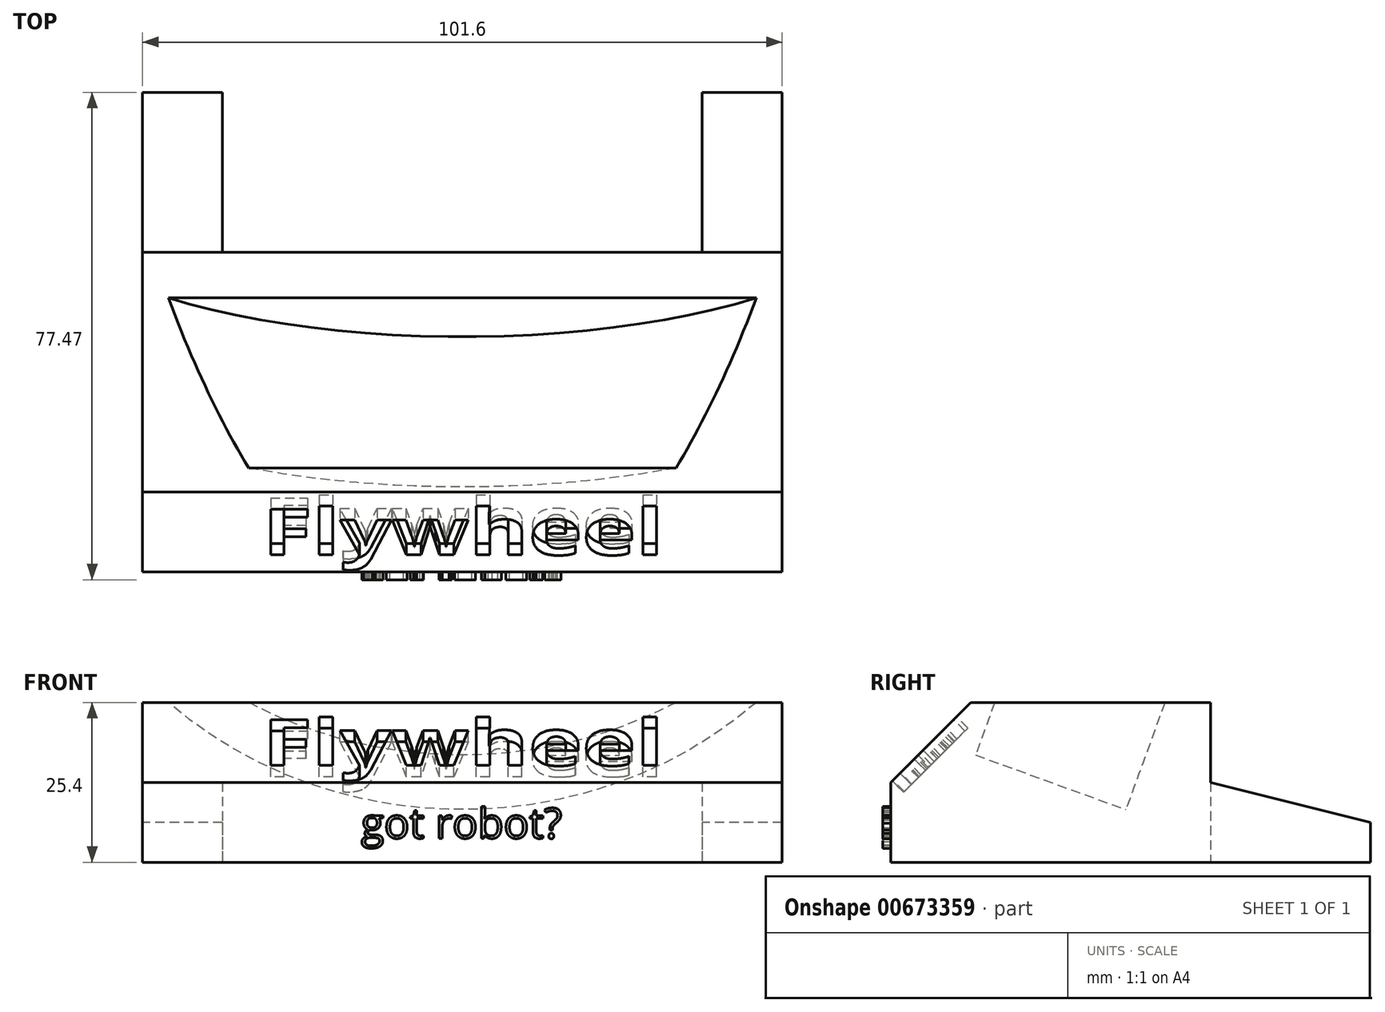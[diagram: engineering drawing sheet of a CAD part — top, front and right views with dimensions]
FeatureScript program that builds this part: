
annotation { "Feature Type Name" : "Feature", "Feature Type Description" : "" }
export const myFeature = defineFeature(function(context is Context, id is Id, definition is map)
    precondition{}
    {
        {
            var Q0;
            Q0=qCreatedBy(makeId("Top.planeOp"),FACE);
            var sketch = newSketch(context, id + "F0", { "sketchPlane" : qUnion([Q0])});
            skLineSegment(sketch, "E0.bottom", {"start": v(-50.8, 25.4) * mm, "end": v(50.8, 25.4) * mm});
            skLineSegment(sketch, "E0.top", {"start": v(-50.8, -25.4) * mm, "end": v(50.8, -25.4) * mm});
            skLineSegment(sketch, "E0.left", {"start": v(-50.8, 25.4) * mm, "end": v(-50.8, -25.4) * mm});
            skLineSegment(sketch, "E0.right", {"start": v(50.8, 25.4) * mm, "end": v(50.8, -25.4) * mm});
            skPoint(sketch, "E0.middle", {"position": v(0, 0) * mm});
            skLineSegment(sketch, "E1.top", {"start": v(-50.8, 0) * mm, "end": v(50.8, 0) * mm});
            skLineSegment(sketch, "E1.left", {"start": v(-50.8, 25.4) * mm, "end": v(-50.8, 0) * mm});
            skLineSegment(sketch, "E1.right", {"start": v(50.8, 25.4) * mm, "end": v(50.8, 0) * mm});
            skLineSegment(sketch, "E2.bottom", {"start": v(-38.1, 25.4) * mm, "end": v(38.1, 25.4) * mm});
            skLineSegment(sketch, "E2.top", {"start": v(-38.1, 50.8) * mm, "end": v(38.1, 50.8) * mm});
            skLineSegment(sketch, "E2.left", {"start": v(-38.1, 25.4) * mm, "end": v(-38.1, 50.8) * mm});
            skLineSegment(sketch, "E2.right", {"start": v(38.1, 25.4) * mm, "end": v(38.1, 50.8) * mm});
            skPoint(sketch, "E2.middle", {"position": v(0, 38.1) * mm});
            skSolve(sketch);
        }
        {
            var Q0;
            {var subQ0=sQuery(id+"F0.wireOp",EDGE,"E0.top");Q0=makeQuery(id+"F0.imprint","IMPRINT",FACE,{"disambiguationData":[TD([[makeQuery(id+"F0.imprint","IMPRINT",EDGE,{"derivedFrom":subQ0}),1.0]])]});}
            var Q1;
            {var subQ3=sQuery(id+"F0.wireOp",EDGE,"E1.top");Q1=makeQuery(id+"F0.imprint","IMPRINT",FACE,{"disambiguationData":[TD([[makeQuery(id+"F0.imprint","IMPRINT",EDGE,{"derivedFrom":subQ3}),1.0]])]});}
            extrude(context, id + "F1", {"entities" : qUnion([Q0, Q1]), "depth" : 25.4 * mm, "offsetDistance" : 25.4 * mm});
        }
        {
            var Q0;
            Q0=qCreatedBy(makeId("Right.planeOp"),FACE);
            var sketch = newSketch(context, id + "F2", { "sketchPlane" : qUnion([Q0])});
            skLineSegment(sketch, "E3", {"start": v(0, 0) * mm, "end": v(0, 12.7) * mm});
            skLineSegment(sketch, "E4", {"start": v(0, 12.7) * mm, "end": v(23.67, 77.74) * mm});
            skLineSegment(sketch, "E5", {"start": v(23.67, 77.74) * mm, "end": v(11.74, 82.08) * mm});
            skLineSegment(sketch, "E6", {"start": v(23.67, 77.74) * mm, "end": v(35.6, 73.4) * mm});
            skLineSegment(sketch, "E7", {"start": v(0, 12.7) * mm, "end": v(11.93, 8.36) * mm});
            skLineSegment(sketch, "E8", {"start": v(11.93, 8.36) * mm, "end": v(35.6, 73.4) * mm});
            skLineSegment(sketch, "E9", {"start": v(0, 12.7) * mm, "end": v(-11.93, 17.04) * mm});
            skLineSegment(sketch, "E10", {"start": v(-11.93, 17.04) * mm, "end": v(11.74, 82.08) * mm});
            skSolve(sketch);
        }
        {
            var Q0;
            Q0=makeQuery(id+"F2.imprint","IMPRINT",FACE,{"disambiguationData":[TD([[makeQuery(id+"F2.imprint","IMPRINT",EDGE,{"derivedFrom":sQuery(id+"F2.wireOp",EDGE,"E4")}),1.0]])]});
            var Q1;
            Q1=makeQuery(id+"F2.imprint","IMPRINT",FACE,{"disambiguationData":[TD([[makeQuery(id+"F2.imprint","IMPRINT",EDGE,{"derivedFrom":sQuery(id+"F2.wireOp",EDGE,"E4")}),-1.0]])]});
            var Q2;
            Q2=sQuery(id+"F2.wireOp",EDGE,"E6");
            revolve(context, id + "F3", {"operationType" : NewBodyOperationType.REMOVE, "entities" : qUnion([Q0, Q1]), "axis" : qUnion([Q2]), "revolveType" : RevolveType.FULL, "oppositeDirection" : true});
        }
        {
            var Q0;
            Q0=makeQuery(id+"F1.opExtrude","CAP_EDGE",EDGE,{"disambiguationData":[OSD([sQuery(id+"F0.wireOp",EDGE,"E0.top")])],"isStart":false});
            chamfer(context, id + "F4", {"entities" : qUnion([Q0]), "width" : 12.7 * mm, "tangentPropagation" : true});
        }
        {
            var Q0;
            Q0=makeQuery(id+"F1.opExtrude","SWEPT_FACE",FACE,{"disambiguationData":[OSD([sQuery(id+"F0.wireOp",EDGE,"E0.left")])]});
            var sketch = newSketch(context, id + "F5", { "sketchPlane" : qUnion([Q0])});
            skLineSegment(sketch, "E11", {"start": v(-25.4, 0) * mm, "end": v(-50.8, 0) * mm});
            skLineSegment(sketch, "E12", {"start": v(-50.8, 0) * mm, "end": v(-50.8, 6.35) * mm});
            skLineSegment(sketch, "E13", {"start": v(-50.8, 6.35) * mm, "end": v(-25.4, 12.7) * mm});
            skSolve(sketch);
        }
        {
            var Q0;
            {var subQ0=sQuery(id+"F5.wireOp",EDGE,"E11");Q0=makeQuery(id+"F5.imprint","IMPRINT",FACE,{"disambiguationData":[TD([[makeQuery(id+"F5.imprint","IMPRINT",EDGE,{"derivedFrom":subQ0}),-1.0]])]});}
            var Q1;
            Q1=makeQuery(id+"F1.opExtrude","SWEPT_FACE",FACE,{"disambiguationData":[OSD([sQuery(id+"F0.wireOp",EDGE,"E0.right")])]});
            extrude(context, id + "F6", {"entities" : qUnion([Q0]), "operationType" : NewBodyOperationType.ADD, "endBound" : BoundingType.UP_TO_SURFACE, "oppositeDirection" : true, "depth" : 25.4 * mm, "endBoundEntityFace" : qUnion([Q1]), "offsetDistance" : 25.4 * mm});
        }
        {
            var Q0;
            Q0=makeQuery(id+"F0.imprint","IMPRINT",FACE,{"disambiguationData":[TD([[makeQuery(id+"F0.imprint","IMPRINT",EDGE,{"derivedFrom":sQuery(id+"F0.wireOp",EDGE,"E2.top")}),-1.0]])]});
            extrude(context, id + "F7", {"entities" : qUnion([Q0]), "operationType" : NewBodyOperationType.REMOVE, "depth" : 25.4 * mm, "offsetDistance" : 25.4 * mm});
        }
        {
            var Q0;
            Q0=makeQuery(id+"F4.opChamfer","BLEND_FACE",FACE,{"disambiguationData":[OSD([sQuery(id+"F0.wireOp",EDGE,"E0.top")])]});
            var sketch = newSketch(context, id + "F8", { "sketchPlane" : qUnion([Q0])});
            skText(sketch, "E14", { "text": "Flywheel", "fontName": "OpenSans-Bold.ttf"});
            const initialGuessF8  = {"E14": [-0.03175, -0.00519, 1, 0, 0.01037]};
            skSetInitialGuess(sketch, initialGuessF8);
            skSolve(sketch);
        }
        {
            var Q0;
            Q0 = qSketchRegion(id + "F8", true);
            extrude(context, id + "F9", {"entities" : qUnion([Q0]), "operationType" : NewBodyOperationType.REMOVE, "oppositeDirection" : true, "depth" : 2.54 * mm, "offsetDistance" : 25.4 * mm});
        }
        {
            var Q0;
            Q0=makeQuery(id+"F1.opExtrude","SWEPT_FACE",FACE,{"disambiguationData":[OSD([sQuery(id+"F0.wireOp",EDGE,"E0.top")])]});
            var sketch = newSketch(context, id + "F10", { "sketchPlane" : qUnion([Q0])});
            skText(sketch, "E15", { "text": "got robot?", "fontName": "OpenSans-Regular.ttf"});
            const initialGuessF10  = {"E15": [-0.01609, 0.00381, 1, 0, 0.00481]};
            skSetInitialGuess(sketch, initialGuessF10);
            skSolve(sketch);
        }
        {
            var Q0;
            Q0 = qSketchRegion(id + "F10", true);
            extrude(context, id + "F11", {"entities" : qUnion([Q0]), "operationType" : NewBodyOperationType.ADD, "depth" : 1.27 * mm, "offsetDistance" : 25.4 * mm});
        }
    });
